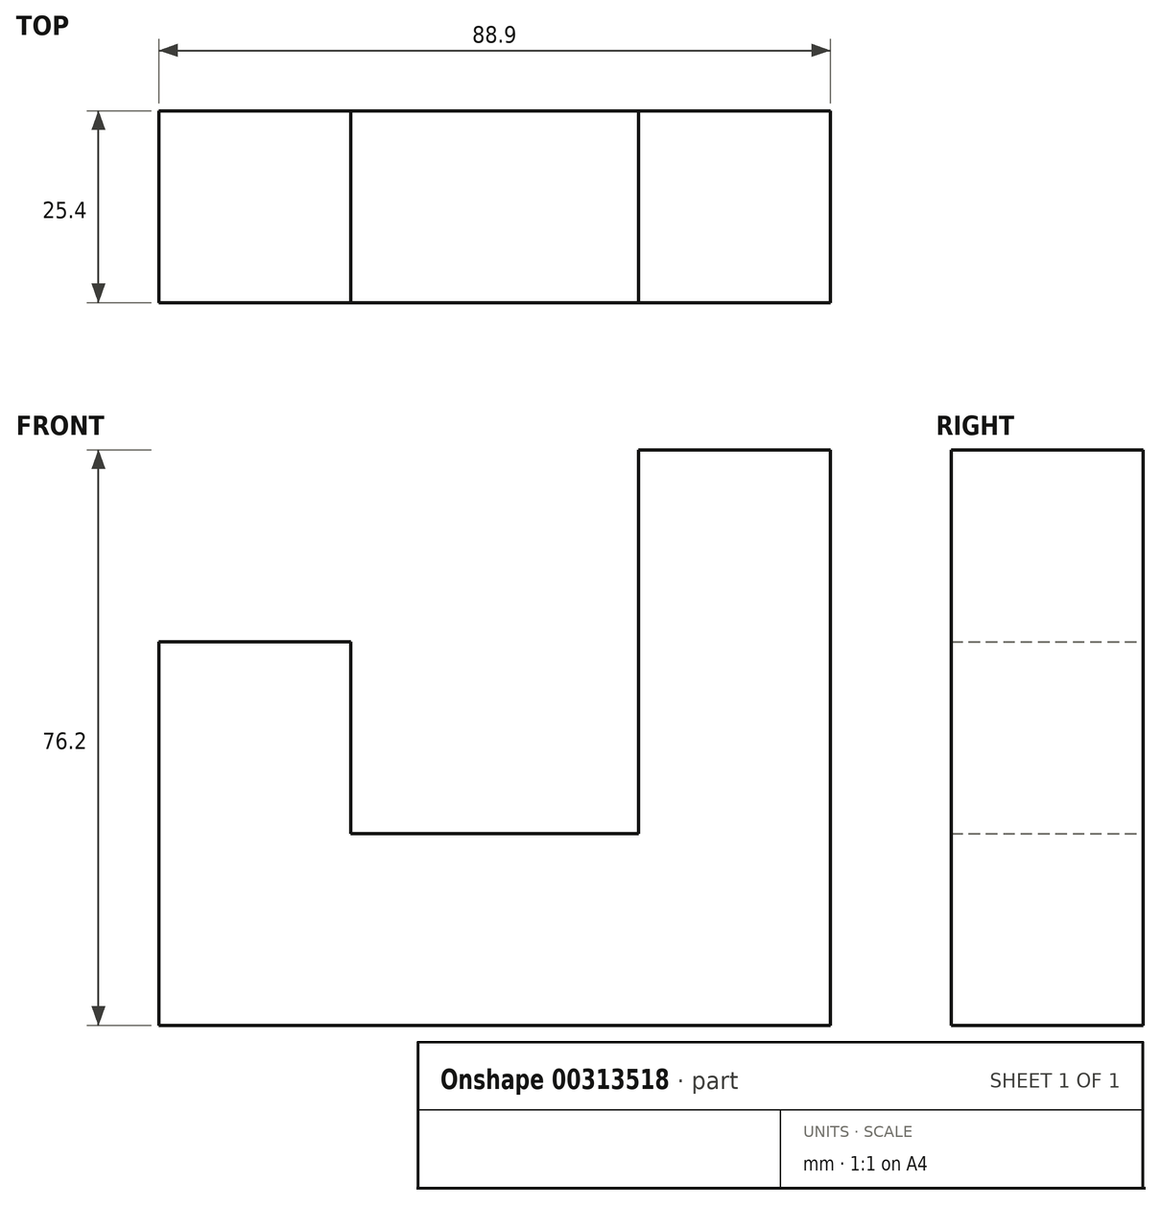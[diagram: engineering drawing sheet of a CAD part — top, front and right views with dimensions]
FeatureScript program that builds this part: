
annotation { "Feature Type Name" : "Feature", "Feature Type Description" : "" }
export const myFeature = defineFeature(function(context is Context, id is Id, definition is map)
    precondition{}
    {
        {
            var Q0;
            Q0=qCreatedBy(makeId("Front.planeOp"),FACE);
            var sketch = newSketch(context, id + "F0", { "sketchPlane" : qUnion([Q0])});
            skLineSegment(sketch, "E0", {"start": v(-48.54, 6.85) * mm, "end": v(-48.54, -43.95) * mm});
            skLineSegment(sketch, "E1", {"start": v(-48.54, -43.95) * mm, "end": v(40.36, -43.95) * mm});
            skLineSegment(sketch, "E2", {"start": v(40.36, -43.95) * mm, "end": v(40.36, 32.25) * mm});
            skLineSegment(sketch, "E3", {"start": v(40.36, 32.25) * mm, "end": v(14.96, 32.25) * mm});
            skLineSegment(sketch, "E4", {"start": v(14.96, 32.25) * mm, "end": v(14.96, -18.55) * mm});
            skLineSegment(sketch, "E5", {"start": v(14.96, -18.55) * mm, "end": v(-23.14, -18.55) * mm});
            skLineSegment(sketch, "E6", {"start": v(-23.14, -18.55) * mm, "end": v(-23.14, 6.85) * mm});
            skLineSegment(sketch, "E7", {"start": v(-23.14, 6.85) * mm, "end": v(-48.54, 6.85) * mm});
            skSolve(sketch);
        }
        {
            var Q0;
            Q0=makeQuery(id+"F0.imprint","IMPRINT",FACE,{"disambiguationData":[TD([[makeQuery(id+"F0.imprint","IMPRINT",EDGE,{"derivedFrom":sQuery(id+"F0.wireOp",EDGE,"E0")}),1.0]])]});
            extrude(context, id + "F1", {"entities" : qUnion([Q0]), "depth" : 25.4 * mm});
        }
    });
